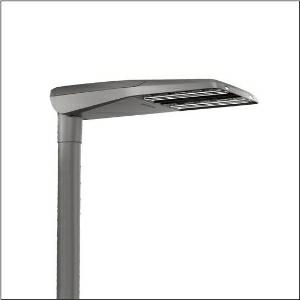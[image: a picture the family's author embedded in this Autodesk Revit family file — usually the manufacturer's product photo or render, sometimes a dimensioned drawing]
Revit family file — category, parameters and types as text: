
# Revit family: streetlight_sl_11_iq_midi___st1_0a_5xc3m51f08le_689c
name_source: partatom
category: Lighting Fixtures
units: mm (PartAtom-declared; Revit-internal decimal feet)

## family parameters
Cut with Voids When Loaded = No
Host = Face
Light Source = No
Part Type = Normal
Room Calculation Point = No
Round Connector Dimension = Use Diameter
Shared = No

## types (1)
- --- (1 x LED, 8920 lm, 60.4 W, 3000K)
    Apparent Load = 60 VA
    CIE Flux Codes = 33 66 96 100 100
    Color Rendering = 70
    Color Temperature = 3000K
    Default Elevation = 1800 mm
    Description = Streetlight SL 11 iQ midi, mast luminaire, primary light control with 3 zone facetted reflector, of plastic, silver coated, highly specular, primary optical cover: cover, of PMMA, transparent, light distribution: ST1.0a, light emission: direct distribution, primary light characteristic: asymmetric, installation type: post-top, side-entry, lamps: LED, High Power LED, rated values: 8.920lm | 60,4W | 147,7lm/W (begin service life); end service life: 8.920lm | 62,5W; at 50% lumin. flux: 4.460lm | 29,6W | 150,7lm/W, colour temperature: 3000K, colour rendering: CRI > 70, light colour: 730, light setting 1 begin service life: 100% | 8.920lm | 60,4W | 147,7lm/W | 3.000K, light setting 1 end service life: 62,5W, further light settings possible, control: optimised constant luminous flux control (CLO 2.0), Street-Remote, Desk-Remote (wireless, voltage-free reading and setting of iQ features in the workshop via application-optimized NFC function/RFID function), Light-Fading, Smart-Wire, Night-Set, Lumen-Switch, Temp-Guard, Auto-Match, with cable H07RN-F 5x 1.5mm², mains connection: 230..240V, AC, 50/60Hz, connection cable pre-assembled, cable length: 8,5m, luminaire housing, of diecast aluminium, powder-coated, Siteco® metallic grey (DB 702S), please order mast flange separately, inclination adjustable without tools: 0°, 5°, 10°, 15° (post-top) | 0°, -5°, -10°, -15° (side-entry), sealing non-destructively replaceable, multi-level sealing system, length: 780mm, width: 376mm, height: 118mm, mast flange for spigot size: 42mm (side-entry): 5XC10008XM4, 60/48mm (side-entry/post-top): 5XC10108XM2, 76/60mm (side-entry/post-top): 5XC10108XM1, equipment: standard, protection rating (complete): IP66, insulation class (complete): insulation class II (safety insulation), certification: CE, ENEC, ENEC+, VDE, impact resistance: IK10, permissible operating ambient temperature for outdoor applications: -25..+50°C, standard-compliant lighting for roads and squares, Environmental Product Declaration (EPD) tested and certified by an independent institute, packaging unit: 1 piece

Light Distribution: ST1.0a
    Height = 118 mm
    Lamp = 1 x LED
    Lamp Light Flux = 8920 lm
    Lamp Power = 60.4 W
    Lamp count = 1
    Length = 780 mm
    Luminous efficacy = 148 lm/W
    Manufacturer = Siteco
    ModVariant = No
    Model = 5XC3M51F08LE
    Number of Poles = 1
    OnlyDefault = Yes
    Power Factor = 1
    Product Name = Streetlight SL 11 iQ midi | ST1.0a
    Product group = mast luminaire | pylon top
    ProductGroupID = 6100
    Protection Class = Protection class II
    Protection Degree = IP 66
    RLX_Detail_Level = 1
    RLX_Emergency_Light_Flux = 0 lm
    RLX_Emergency_Type = 0
    RLX_Emergency_Type_DB = No
    RlxData = <blob elided: 70277 chars, md5=91e1a208>
    Socket = socket
    Standby Power = 0 W
    System Light Flux = 8920 lm
    System Power = 60 W
    Type Comments = factory setting: luminous flux: 100 % | dim-lin: 254 | 520 mA
    Type Image = l_1005960.jpg
    URL = http://relux.com
    VarID = @adj_110045
    Voltage = 0 V
    Weight = 0.00 kg
    Width = 376 mm

## geometry (parser evidence)
native form markers: Blend x4, Sweep x10
no freeform markers — native parametric forms only
